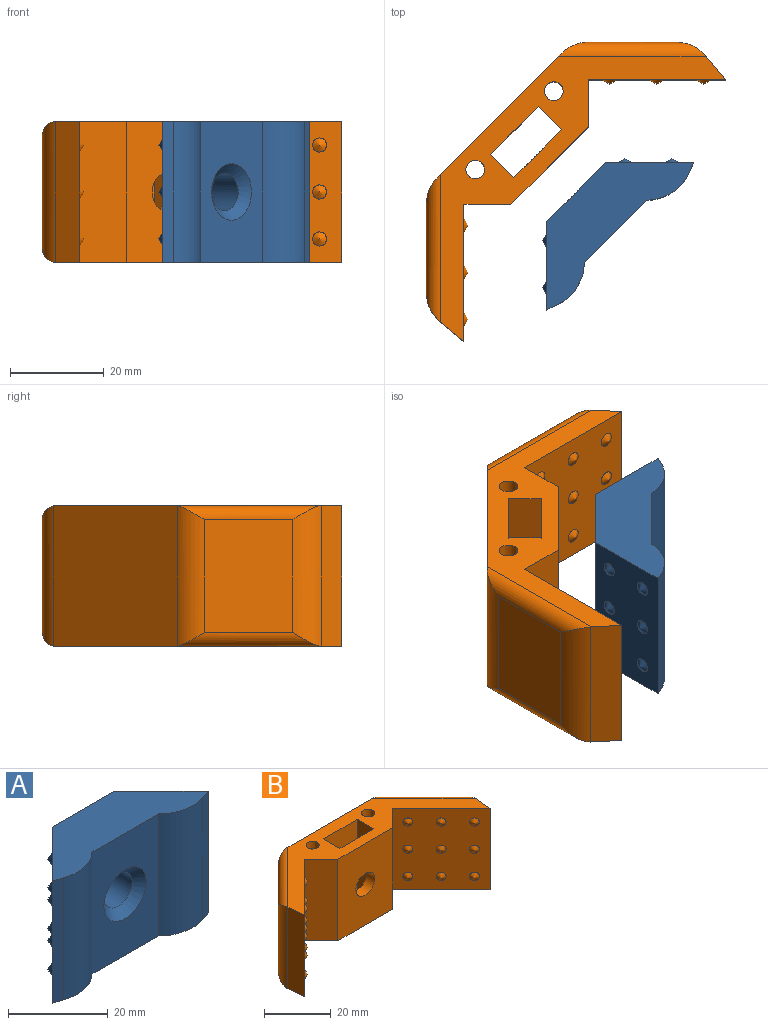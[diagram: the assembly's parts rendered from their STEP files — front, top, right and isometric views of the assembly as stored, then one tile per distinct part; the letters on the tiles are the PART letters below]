
ASSEMBLY  parts=2 mates=1
PART A: 24 faces, bbox 44.3x14.7x30 mm
  f0: plane 30x18.77mm, normal (0,-1,0), area 450mm2, adj f6,f7,f9,f10,f11
  f1: plane 30x2.37mm, normal (0.34,-0.94,0), area 75.6mm2, adj f2,f6,f7,f11
  f2: plane 30x13.29mm, normal (0.71,0.71,0), area 521.2mm2, adj f1,f3,f6,f7,f18,f19,f20,f21
  f3: plane 30x17.74mm, normal (0,1,0), area 481.8mm2, adj f2,f4,f6,f7,f8
  f4: plane 30x13.29mm, normal (-0.71,0.71,0), area 521.2mm2, adj f3,f5,f6,f7,f12,f13,f14,f15
  f5: plane 30x2.37mm, normal (-0.34,-0.94,0), area 75.6mm2, adj f4,f6,f7,f10
  f6: plane 44.31x14.72mm, normal (0,0,1), area 402.7mm2, adj f0,f1,f2,f3,f4,f5,f10,f11
  f7: plane 44.31x14.72mm, normal (0,0,-1), area 402.7mm2, adj f0,f1,f2,f3,f4,f5,f10,f11
  f8: cylinder r=4mm len=9.83mm, axis (0,-1,0), area 247.1mm2, adj f3,f9
  f9: cone r=4mm half-angle=45deg, axis (0,-1,0), area 88.9mm2, adj f0,f8
  f10: cylinder r=10mm len=30mm, axis (0,0,1), area 336.9mm2, adj f0,f5,f6,f7
  f11: cylinder r=10mm len=30mm, axis (0,0,1), area 336.9mm2, adj f0,f1,f6,f7
  f12: cone r=1.5mm half-angle=60deg, axis (0.71,-0.71,0), area 8.2mm2, adj f4
  f13: cone r=1.5mm half-angle=60deg, axis (0.71,-0.71,0), area 8.2mm2, adj f4
  f14: cone r=1.5mm half-angle=60deg, axis (0.71,-0.71,0), area 8.2mm2, adj f4
  f15: cone r=1.5mm half-angle=60deg, axis (0.71,-0.71,0), area 8.2mm2, adj f4
  f16: cone r=1.5mm half-angle=60deg, axis (0.71,-0.71,0), area 8.2mm2, adj f4
  f17: cone r=1.5mm half-angle=60deg, axis (0.71,-0.71,0), area 8.2mm2, adj f4
  f18: cone r=1.5mm half-angle=60deg, axis (-0.71,-0.71,0), area 8.2mm2, adj f2
  f19: cone r=1.5mm half-angle=60deg, axis (-0.71,-0.71,0), area 8.2mm2, adj f2
  f20: cone r=1.5mm half-angle=60deg, axis (-0.71,-0.71,0), area 8.2mm2, adj f2
  f21: cone r=1.5mm half-angle=60deg, axis (-0.71,-0.71,0), area 8.2mm2, adj f2
  f22: cone r=1.5mm half-angle=60deg, axis (-0.71,-0.71,0), area 8.2mm2, adj f2
  f23: cone r=1.5mm half-angle=60deg, axis (-0.71,-0.71,0), area 8.2mm2, adj f2
PART B: 47 faces, bbox 84.2x30.8x30 mm
  f0: plane 30x6.64mm, normal (1,-0.09,0), area 200.1mm2, adj f13,f16,f17,f21,f27,f28
  f1: plane 24x13.31mm, normal (0.71,0.71,0), area 451.6mm2, adj f21,f22,f27,f28
  f2: plane 37.46x30mm, normal (0,1,0), area 1123.6mm2, adj f16,f17,f22,f23,f25,f26,f27,f28
  f3: plane 24x13.31mm, normal (-0.71,0.71,0), area 451.6mm2, adj f23,f24,f25,f26
  f4: plane 30x6.64mm, normal (-1,-0.09,0), area 200.1mm2, adj f5,f16,f17,f24,f25,f26
  f5: plane 30x20.67mm, normal (0.71,-0.71,0), area 813.4mm2, adj f4,f6,f16,f17,f29,f30,f31,f32
  f6: plane 30x7.07mm, normal (-0.71,-0.71,0), area 300mm2, adj f5,f7,f16,f17
  f7: plane 30x23.31mm, normal (0,-1,0), area 649.1mm2, adj f6,f8,f16,f17,f20
  f8: plane 30x7.07mm, normal (0.71,-0.71,0), area 300mm2, adj f7,f13,f16,f17
  f9: plane 30x7mm, normal (-1,0,0), area 210mm2, adj f10,f14,f16,f17
  f10: plane 30x14.4mm, normal (0,1,0), area 381.7mm2, adj f9,f11,f16,f17,f20
  f11: plane 30x7mm, normal (1,0,0), area 210mm2, adj f10,f14,f16,f17
  f12: cylinder r=2mm len=30mm, axis (0,0,-1), area 377mm2, adj f16,f17
  f13: plane 30x20.67mm, normal (-0.71,-0.71,0), area 813.4mm2, adj f0,f8,f16,f17,f38,f39,f40,f41
  f14: plane 30x14.4mm, normal (0,-1,0), area 381.7mm2, adj f9,f11,f16,f17,f19
  f15: cylinder r=2mm len=30mm, axis (0,0,-1), area 377mm2, adj f16,f17
  f16: plane 79.97x28.67mm, normal (0,0,1), area 684.2mm2, adj f0,f2,f4,f5,f6,f7,f8,f9
  f17: plane 79.97x28.67mm, normal (0,0,-1), area 684.2mm2, adj f0,f2,f4,f5,f6,f7,f8,f9
  f18: cone r=0mm half-angle=59deg, axis (0,-1,0), area 58.6mm2, adj f19
  f19: cylinder r=4mm len=8mm, axis (0,-1,0), area 27mm2, adj f14,f18
  f20: cylinder r=4mm len=8mm, axis (0,-1,0), area 89.8mm2, adj f7,f10
  f21: cylinder r=8mm len=30mm, axis (0,0,-1), area 193.8mm2, adj f0,f1,f27,f28
  f22: cylinder r=8mm len=29.85mm, axis (0,0,-1), area 172.1mm2, adj f1,f2,f27,f28
  f23: cylinder r=8mm len=29.85mm, axis (0,0,1), area 172.1mm2, adj f2,f3,f25,f26
  f24: cylinder r=8mm len=30mm, axis (0,0,-1), area 193.8mm2, adj f3,f4,f25,f26
  f25: cylinder r=3mm len=24.31mm, axis (0.71,0.71,0), area 121.4mm2, adj f2,f3,f4,f16,f23,f24
  f26: cylinder r=3mm len=24.31mm, axis (-0.71,-0.71,0), area 121.4mm2, adj f2,f3,f4,f17,f23,f24
  f27: cylinder r=3mm len=24.31mm, axis (0.71,-0.71,0), area 121.4mm2, adj f0,f1,f2,f16,f21,f22
  f28: cylinder r=3mm len=24.31mm, axis (-0.71,0.71,0), area 121.4mm2, adj f0,f1,f2,f17,f21,f22
  f29: cone r=1.5mm half-angle=60deg, axis (-0.71,0.71,0), area 8.2mm2, adj f5
  f30: cone r=1.5mm half-angle=60deg, axis (-0.71,0.71,0), area 8.2mm2, adj f5
  f31: cone r=1.5mm half-angle=60deg, axis (-0.71,0.71,0), area 8.2mm2, adj f5
  f32: cone r=1.5mm half-angle=60deg, axis (-0.71,0.71,0), area 8.2mm2, adj f5
  f33: cone r=1.5mm half-angle=60deg, axis (-0.71,0.71,0), area 8.2mm2, adj f5
  f34: cone r=1.5mm half-angle=60deg, axis (-0.71,0.71,0), area 8.2mm2, adj f5
  f35: cone r=1.5mm half-angle=60deg, axis (-0.71,0.71,0), area 8.2mm2, adj f5
  f36: cone r=1.5mm half-angle=60deg, axis (-0.71,0.71,0), area 8.2mm2, adj f5
  f37: cone r=1.5mm half-angle=60deg, axis (-0.71,0.71,0), area 8.2mm2, adj f5
  f38: cone r=1.5mm half-angle=60deg, axis (0.71,0.71,0), area 8.2mm2, adj f13
  f39: cone r=1.5mm half-angle=60deg, axis (0.71,0.71,0), area 8.2mm2, adj f13
  f40: cone r=1.5mm half-angle=60deg, axis (0.71,0.71,0), area 8.2mm2, adj f13
  f41: cone r=1.5mm half-angle=60deg, axis (0.71,0.71,0), area 8.2mm2, adj f13
  f42: cone r=1.5mm half-angle=60deg, axis (0.71,0.71,0), area 8.2mm2, adj f13
  f43: cone r=1.5mm half-angle=60deg, axis (0.71,0.71,0), area 8.2mm2, adj f13
  f44: cone r=1.5mm half-angle=60deg, axis (0.71,0.71,0), area 8.2mm2, adj f13
  f45: cone r=1.5mm half-angle=60deg, axis (0.71,0.71,0), area 8.2mm2, adj f13
  f46: cone r=1.5mm half-angle=60deg, axis (0.71,0.71,0), area 8.2mm2, adj f13
PLACE A rot(axis=(0,0,1),45deg) t=(-238.46,-203.73,187.91)mm
PLACE B rot(axis=(0.38,-0.92,0),180deg) t=(-238.09,-204.1,217.91)mm
MATE fastened A.f8 <-> B.f18  axis (-0.71,0.71,0) through (-236.43,-205.76,202.91)mm
